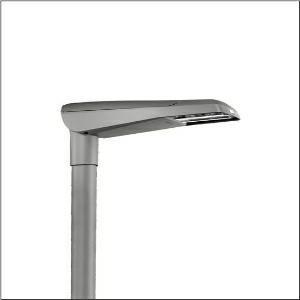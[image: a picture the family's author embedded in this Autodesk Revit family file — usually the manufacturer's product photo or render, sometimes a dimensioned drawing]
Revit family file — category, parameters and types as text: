
# Revit family: streetlight_sl_11_iq_micro___st1_2a_5xc1a21f08ce_ee83
name_source: partatom
category: Lighting Fixtures
units: mm (PartAtom-declared; Revit-internal decimal feet)

## family parameters
Cut with Voids When Loaded = No
Host = Face
Light Source = No
Part Type = Normal
Room Calculation Point = No
Round Connector Dimension = Use Diameter
Shared = No

## types (1)
- --- (1 x LED, 1540 lm, 12.6 W, 2200K)
    Apparent Load = 13 VA
    CIE Flux Codes = 33 71 96 100 100
    Color Rendering = 70
    Color Temperature = 2200K
    Default Elevation = 1800 mm
    Description = Streetlight SL 11 iQ micro, mast luminaire, primary light control with 3 zone facetted reflector, of plastic, silver coated, highly specular, primary optical cover: cover, of PMMA, transparent, light distribution: ST1.2a, light emission: direct distribution, primary light characteristic: asymmetric, installation type: post-top, side-entry, lamps: LED, High Power LED, rated values: 1.540lm | 12,6W | 122,2lm/W (begin service life); end service life: 1.540lm | 12,9W; at 50% lumin. flux: 770lm | 6,8W | 113,2lm/W, colour temperature: 2200K, colour rendering: CRI > 70, light colour: 722, light setting 1 begin service life: 100% | 1.540lm | 12,6W | 122,2lm/W | 2.200K, light setting 1 end service life: 12,9W, further light settings possible, control: Street-Remote, optimised constant luminous flux control (CLO 2.0), Desk-Remote (wireless, voltage-free reading and setting of iQ features in the workshop via application-optimized NFC function/RFID function), Light-Fading, Smart-Wire, Night-Set, Lumen-Switch, Temp-Guard, Auto-Match, with cable H07RN-F 3x 1.5mm², mains connection: 230..240V, AC, 50/60Hz, connection cable pre-assembled, cable length: 5,5m, luminaire housing, of diecast aluminium, powder-coated, SITECO metallic grey (DB 702S), please order mast flange separately, inclination adjustable without tools: 0°, 5°, 10°, 15° (post-top) | 0°, -5°, -10°, -15° (side-entry), sealing non-destructively replaceable, multi-level sealing system, length: 600mm, width: 174mm, height: 116mm, mast flange for spigot size: 42mm (side-entry): 5XC10008XM4, 60/48mm (side-entry/post-top): 5XC10108XM2, 76/60mm (side-entry/post-top): 5XC10108XM1, equipment: standard, protection rating (complete): IP66, insulation class (complete): insulation class II (safety insulation), certification: CE, ENEC, ENEC+, VDE, impact resistance: IK10, permissible operating ambient temperature for outdoor applications: -25..+50°C, standard-compliant lighting for roads and squares, Environmental Product Declaration (EPD) tested and certified by an independent institute, packaging unit: 1 piece

Light Distribution: ST1.2a
    Height = 116 mm
    Lamp = 1 x LED
    Lamp Light Flux = 1540 lm
    Lamp Power = 12.6 W
    Lamp count = 1
    Length = 600 mm
    Luminous efficacy = 122 lm/W
    Manufacturer = Siteco
    ModVariant = No
    Model = 5XC1A21F08CE
    Number of Poles = 1
    OnlyDefault = Yes
    Power Factor = 1
    Product Name = Streetlight SL 11 iQ micro | ST1.2a
    Product group = mast luminaire | pylon top
    ProductGroupID = 6100
    Protection Class = Protection class II
    Protection Degree = IP 66
    RLX_Detail_Level = 1
    RLX_Emergency_Light_Flux = 0 lm
    RLX_Emergency_Type = 0
    RLX_Emergency_Type_DB = No
    RlxData = <blob elided: 26509 chars, md5=0f8ee701>
    Socket = socket
    Standby Power = 0 W
    System Light Flux = 1540 lm
    System Power = 13 W
    Type Comments = factory setting: luminous flux: 100 % | dim-lin: 254 | 229 mA
    Type Image = l_1006566.jpg
    URL = http://relux.com
    VarID = @adj_019039
    Voltage = 0 V
    Weight = 0.00 kg
    Width = 174 mm

## geometry (parser evidence)
native form markers: Blend x4, Sweep x11
no freeform markers — native parametric forms only
